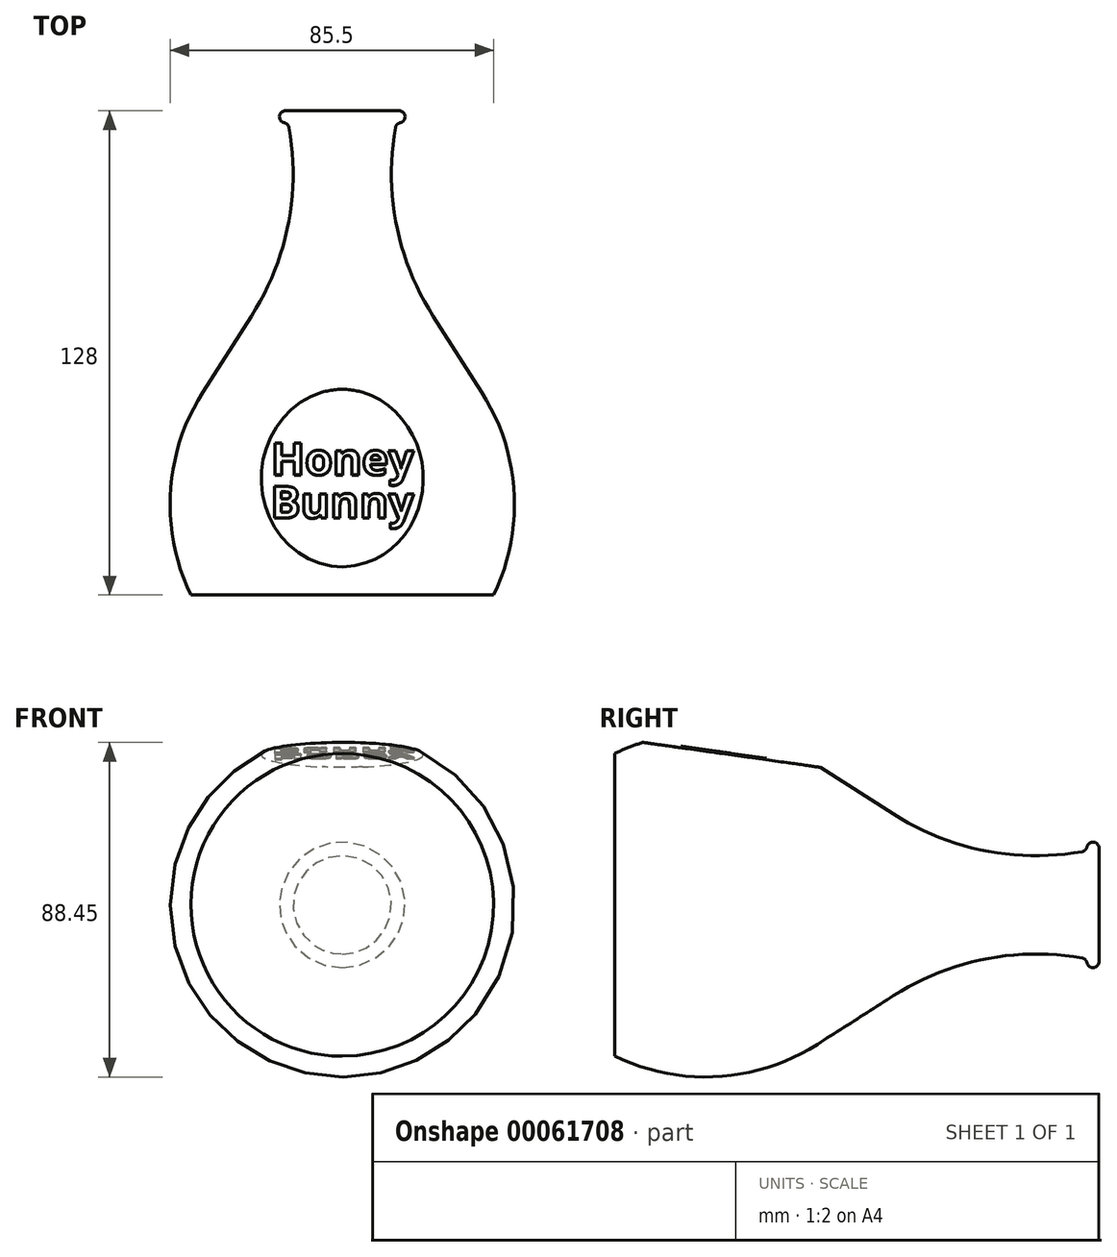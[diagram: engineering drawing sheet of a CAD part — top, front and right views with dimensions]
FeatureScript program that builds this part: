
annotation { "Feature Type Name" : "Feature", "Feature Type Description" : "" }
export const myFeature = defineFeature(function(context is Context, id is Id, definition is map)
    precondition{}
    {
        {
            var Q0;
            Q0=qCreatedBy(makeId("Top.planeOp"),FACE);
            var sketch = newSketch(context, id + "F0", { "sketchPlane" : qUnion([Q0])});
            skLineSegment(sketch, "E0", {"start": v(0, 0) * mm, "end": v(0, 128) * mm});
            skLineSegment(sketch, "E1", {"start": v(0, 128) * mm, "end": v(15, 128) * mm});
            skLineSegment(sketch, "E2", {"start": v(0, 0) * mm, "end": v(40, 0) * mm});
            skArc(sketch, "E3", {"start": v(40, 0) * mm, "mid": v(45.4, 27.2) * mm, "end": v(36.86, 53.56) * mm});
            skArc(sketch, "E4", {"start": v(15, 128) * mm, "mid": v(13.94, 99.94) * mm, "end": v(24, 73.73) * mm});
            skLineSegment(sketch, "E5", {"start": v(24, 73.73) * mm, "end": v(36.86, 53.56) * mm});
            skSolve(sketch);
        }
        {
            var Q0;
            Q0=makeQuery(id+"F0.imprint","IMPRINT",FACE,{"disambiguationData":[TD([[makeQuery(id+"F0.imprint","IMPRINT",EDGE,{"derivedFrom":sQuery(id+"F0.wireOp",EDGE,"E0")}),-1.0]])]});
            var Q1;
            Q1=sQuery(id+"F0.wireOp",EDGE,"E0");
            revolve(context, id + "F1", {"entities" : qUnion([Q0]), "axis" : qUnion([Q1]), "revolveType" : RevolveType.FULL});
        }
        {
            var Q0;
            Q0=qCreatedBy(makeId("Top.planeOp"),FACE);
            var sketch = newSketch(context, id + "F2", { "sketchPlane" : qUnion([Q0])});
            skLineSegment(sketch, "E6", {"start": v(0, 128) * mm, "end": v(-15, 128) * mm});
            skArc(sketch, "E7", {"start": v(-15, 128) * mm, "mid": v(-16.6, 126.4) * mm, "end": v(-15, 124.8) * mm});
            skLineSegment(sketch, "E8", {"start": v(-15, 124.8) * mm, "end": v(0, 124.8) * mm});
            skLineSegment(sketch, "E9", {"start": v(0, 124.8) * mm, "end": v(0, 128) * mm});
            skSolve(sketch);
        }
        {
            var Q0;
            Q0=makeQuery(id+"F2.imprint","IMPRINT",FACE,{"disambiguationData":[TD([[makeQuery(id+"F2.imprint","IMPRINT",EDGE,{"derivedFrom":sQuery(id+"F2.wireOp",EDGE,"E6")}),1.0]])]});
            var Q1;
            Q1=sQuery(id+"F2.wireOp",EDGE,"E9");
            revolve(context, id + "F3", {"operationType" : NewBodyOperationType.ADD, "entities" : qUnion([Q0]), "axis" : qUnion([Q1]), "revolveType" : RevolveType.FULL});
        }
        {
            var Q0;
            Q0=makeQuery(id+"F3.boolean.opBoolean","INTERSECT",EDGE,{"derivedFrom":[makeQuery(id+"F1.opRevolve","SWEPT_FACE",FACE,{"disambiguationData":[OSD([sQuery(id+"F0.wireOp",EDGE,"E4")])]}),makeQuery(id+"F3.opRevolve","SWEPT_FACE",FACE,{"disambiguationData":[OSD([sQuery(id+"F2.wireOp",EDGE,"E8")])]})]});
            fillet(context, id + "F4", {"entities" : qUnion([Q0]), "radius" : 1.6 * mm, "tangentPropagation" : true, "allowEdgeOverflow" : false});
        }
        {
            var Q0;
            Q0=qCreatedBy(makeId("Right.planeOp"),FACE);
            var sketch = newSketch(context, id + "F5", { "sketchPlane" : qUnion([Q0])});
            skLineSegment(sketch, "E10", {"start": v(70, 34.16) * mm, "end": v(0, 44) * mm});
            skLineSegment(sketch, "E11", {"start": v(0, 44) * mm, "end": v(0, 60) * mm});
            skLineSegment(sketch, "E12", {"start": v(0, 60) * mm, "end": v(70, 60) * mm});
            skLineSegment(sketch, "E13", {"start": v(70, 60) * mm, "end": v(70, 34.16) * mm});
            skSolve(sketch);
        }
        {
            var Q0;
            Q0=makeQuery(id+"F5.imprint","IMPRINT",FACE,{"disambiguationData":[TD([[makeQuery(id+"F5.imprint","IMPRINT",EDGE,{"derivedFrom":sQuery(id+"F5.wireOp",EDGE,"E10")}),-1.0]])]});
            extrude(context, id + "F6", {"entities" : qUnion([Q0]), "operationType" : NewBodyOperationType.REMOVE, "endBound" : BoundingType.SYMMETRIC, "oppositeDirection" : true, "depth" : 50 * mm});
        }
        {
            var Q0;
            Q0=makeQuery(id+"F6.boolean.opBoolean","COPY",FACE,{"derivedFrom":makeQuery(id+"F6.opExtrude","SWEPT_FACE",FACE,{"disambiguationData":[OSD([sQuery(id+"F5.wireOp",EDGE,"E10")])]})});
            var sketch = newSketch(context, id + "F7", { "sketchPlane" : qUnion([Q0])});
            skText(sketch, "E14", { "text": "Honey", "fontName": "OpenSans-Bold.ttf"});
            const initialGuessF7  = {"E14": [-0.0189, 0.02588, 1, 0, 0.0085]};
            skSetInitialGuess(sketch, initialGuessF7);
            skSolve(sketch);
        }
        {
            var Q0;
            Q0=makeQuery(id+"F7.imprint","IMPRINT",FACE,{"disambiguationData":[TD([[makeQuery(id+"F7.imprint","IMPRINT",EDGE,{"derivedFrom":sQuery(id+"F7.wireOp",EDGE,"E14.sketch_text.stroke-0")}),1.0]])]});
            var sketch = newSketch(context, id + "F8", { "sketchPlane" : qUnion([Q0])});
            skText(sketch, "E15", { "text": "Bunny", "fontName": "OpenSans-Bold.ttf"});
            const initialGuessF8  = {"E15": [-0.01896, 0.01438, 1, 0, 0.0085]};
            skSetInitialGuess(sketch, initialGuessF8);
            skSolve(sketch);
        }
        {
            var Q0;
            Q0 = qSketchRegion(id + "F7", true);
            extrude(context, id + "F9", {"entities" : qUnion([Q0]), "operationType" : NewBodyOperationType.ADD, "depth" : 0.4 * mm});
        }
        {
            var Q0;
            Q0 = qSketchRegion(id + "F8", true);
            extrude(context, id + "F10", {"entities" : qUnion([Q0]), "operationType" : NewBodyOperationType.ADD, "depth" : 0.4 * mm});
        }
    });
